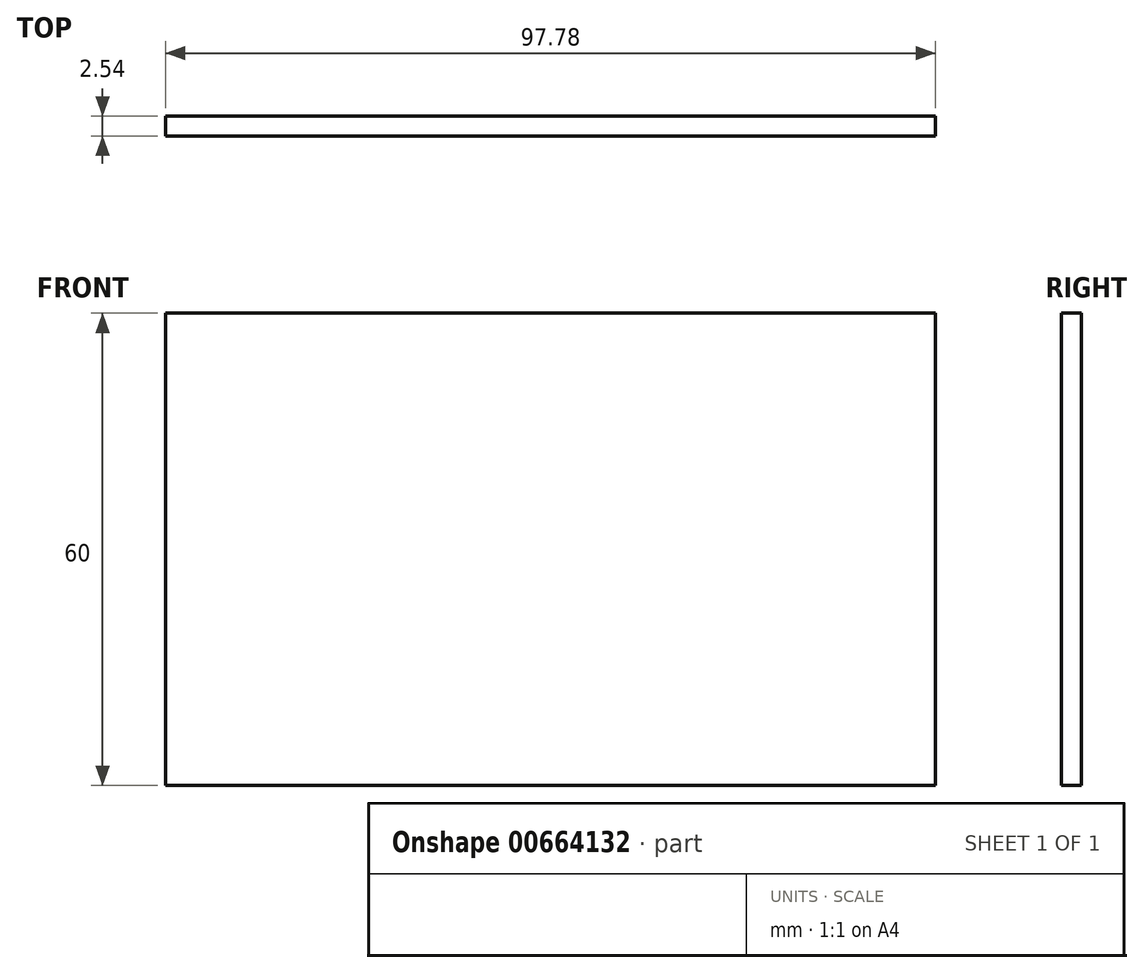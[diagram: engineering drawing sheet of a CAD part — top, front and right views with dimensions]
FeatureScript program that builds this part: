
annotation { "Feature Type Name" : "Feature", "Feature Type Description" : "" }
export const myFeature = defineFeature(function(context is Context, id is Id, definition is map)
    precondition{}
    {
        {
            var Q0;
            Q0=qCreatedBy(makeId("Front.planeOp"),FACE);
            var sketch = newSketch(context, id + "F0", { "sketchPlane" : qUnion([Q0])});
            skLineSegment(sketch, "E0", {"start": v(-97.78, 0) * mm, "end": v(0, 0) * mm});
            skLineSegment(sketch, "E1", {"start": v(-97.78, 0) * mm, "end": v(-97.78, 60) * mm});
            skLineSegment(sketch, "E2", {"start": v(-97.78, 60) * mm, "end": v(0, 60) * mm});
            skLineSegment(sketch, "E3", {"start": v(0, 60) * mm, "end": v(0, 0) * mm});
            skLineSegment(sketch, "E4", {"start": v(-62.18, -3.71) * mm, "end": v(-82.12, -32.25) * mm});
            skLineSegment(sketch, "E5", {"start": v(-62.18, -3.71) * mm, "end": v(-43.67, -32.25) * mm});
            skSolve(sketch);
        }
        {
            var Q0;
            Q0=makeQuery(id+"F0.imprint","IMPRINT",FACE,{"disambiguationData":[TD([[makeQuery(id+"F0.imprint","IMPRINT",EDGE,{"derivedFrom":sQuery(id+"F0.wireOp",EDGE,"E0")}),1.0]])]});
            extrude(context, id + "F1", {"entities" : qUnion([Q0]), "depth" : 2.54 * mm, "offsetDistance" : 25.4 * mm});
        }
    });
